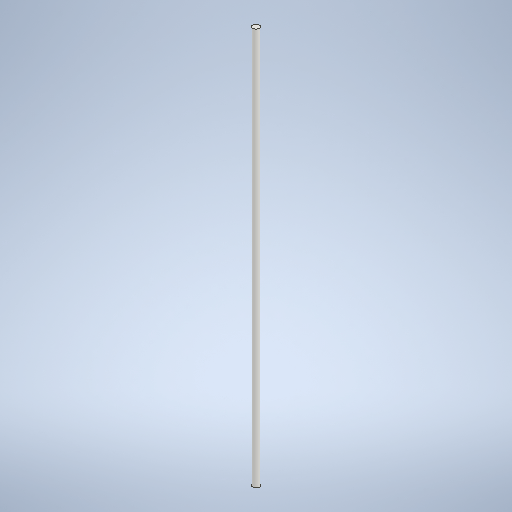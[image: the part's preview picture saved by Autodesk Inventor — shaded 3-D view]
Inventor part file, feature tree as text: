
AUTODESK INVENTOR PART (.ipt)
format: ipt  version: 2025.1 (Build 291241020, 241B)  size: 251,392 bytes
history: native  units: in
note: dims shown in document units (in); Inventor stores cm internally (conversion verified against a paired STEP export)
features: extrude x1, sketch x1
ambient origin geometry x8: Origin, YZ Plane, XZ Plane, XY Plane, X Axis, Y Axis, Z Axis, Center Point
bodies: Solid1 (feature_tree)
feature tree (2):
  extrude  "Extrusion1"  Depth=31.5628in TaperAngle=0.0deg
  sketch  "Sketch1"  dims[d0=0.5in d1=31.5628in d2=0.0in]
